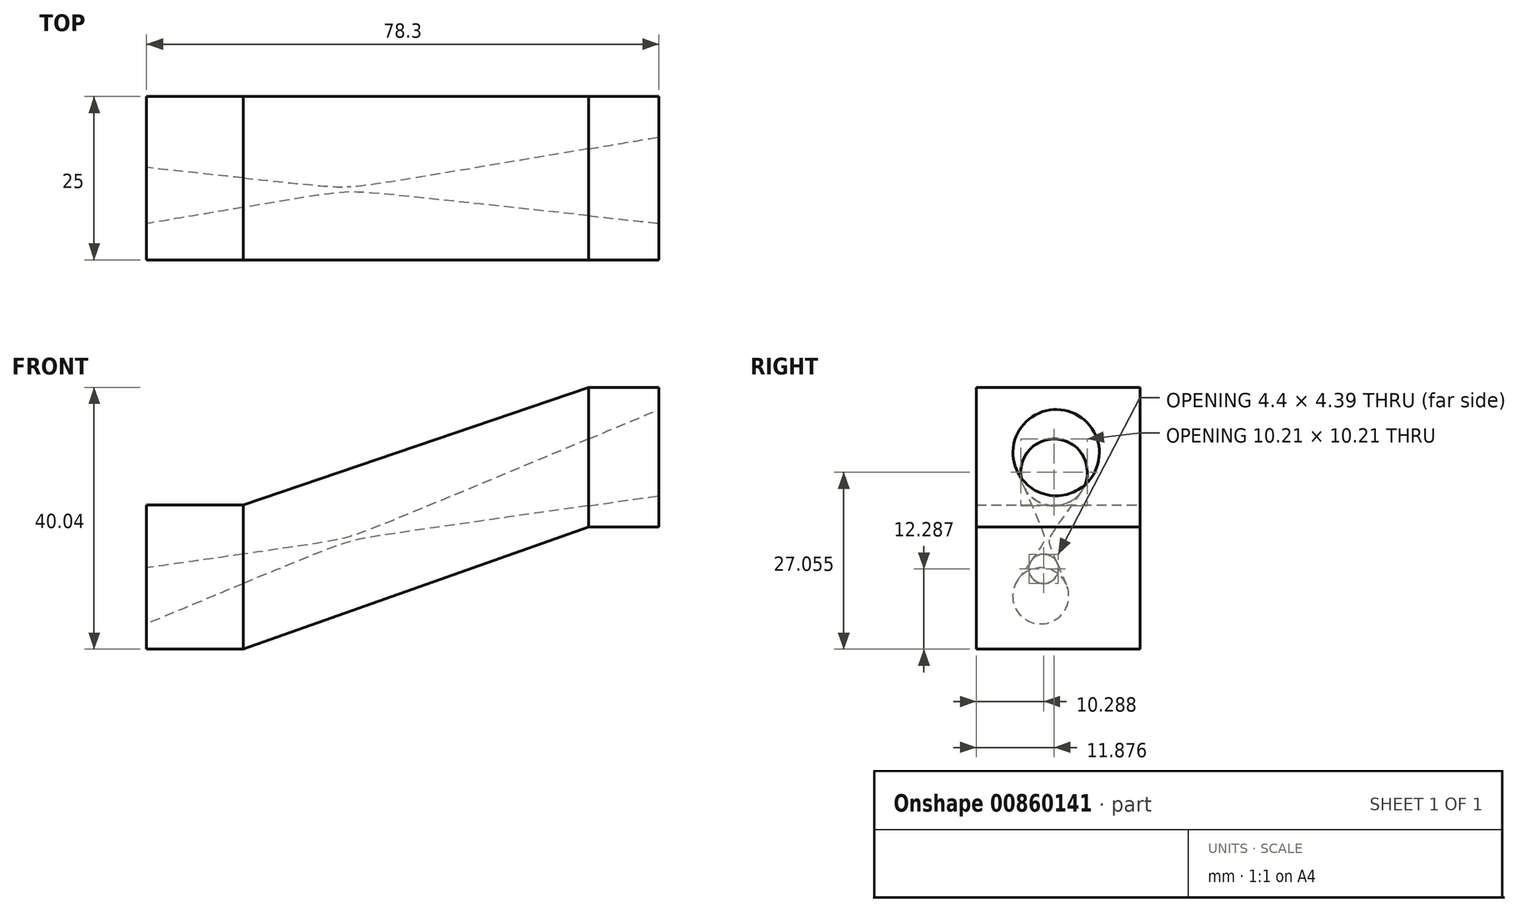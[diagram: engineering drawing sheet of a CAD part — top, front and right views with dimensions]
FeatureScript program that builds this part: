
annotation { "Feature Type Name" : "Feature", "Feature Type Description" : "" }
export const myFeature = defineFeature(function(context is Context, id is Id, definition is map)
    precondition{}
    {
        {
            var Q0;
            Q0=qCreatedBy(makeId("Front.planeOp"),FACE);
            var sketch = newSketch(context, id + "F0", { "sketchPlane" : qUnion([Q0])});
            skLineSegment(sketch, "E0.bottom", {"start": v(-43.84, 22.16) * mm, "end": v(43.84, 22.16) * mm});
            skLineSegment(sketch, "E0.top", {"start": v(-43.84, -22.16) * mm, "end": v(43.84, -22.16) * mm});
            skLineSegment(sketch, "E0.left", {"start": v(-43.84, 22.16) * mm, "end": v(-43.84, -22.16) * mm});
            skLineSegment(sketch, "E0.right", {"start": v(43.84, 22.16) * mm, "end": v(43.84, -22.16) * mm});
            skPoint(sketch, "E0.middle", {"position": v(0, 0) * mm});
            skSolve(sketch);
        }
        {
            var Q0;
            Q0=makeQuery(id+"F0.imprint","IMPRINT",FACE,{"disambiguationData":[TD([[makeQuery(id+"F0.imprint","IMPRINT",EDGE,{"derivedFrom":sQuery(id+"F0.wireOp",EDGE,"E0.bottom")}),-1.0]])]});
            var sketch = newSketch(context, id + "F1", { "sketchPlane" : qUnion([Q0])});
            skLineSegment(sketch, "E1.bottom", {"start": v(28.87, -3.33) * mm, "end": v(39.64, -3.33) * mm});
            skLineSegment(sketch, "E1.top", {"start": v(28.87, 17.99) * mm, "end": v(39.64, 17.99) * mm});
            skLineSegment(sketch, "E1.left", {"start": v(28.87, -3.33) * mm, "end": v(28.87, 17.99) * mm});
            skLineSegment(sketch, "E1.right", {"start": v(39.64, -3.33) * mm, "end": v(39.64, 17.99) * mm});
            skPoint(sketch, "E1.middle", {"position": v(34.26, 7.33) * mm});
            skSolve(sketch);
        }
        {
            var Q0;
            Q0 = qSketchRegion(id + "F1", true);
            extrude(context, id + "F2", {"entities" : qUnion([Q0]), "depth" : 25 * mm, "offsetDistance" : 25 * mm});
        }
        {
            var Q0;
            Q0=makeQuery(id+"F0.imprint","IMPRINT",FACE,{"disambiguationData":[TD([[makeQuery(id+"F0.imprint","IMPRINT",EDGE,{"derivedFrom":sQuery(id+"F0.wireOp",EDGE,"E0.bottom")}),-1.0]])]});
            var sketch = newSketch(context, id + "F3", { "sketchPlane" : qUnion([Q0])});
            skLineSegment(sketch, "E2.bottom", {"start": v(-23.92, 0) * mm, "end": v(-38.66, 0) * mm});
            skLineSegment(sketch, "E2.top", {"start": v(-23.92, -22.05) * mm, "end": v(-38.66, -22.05) * mm});
            skLineSegment(sketch, "E2.left", {"start": v(-23.92, 0) * mm, "end": v(-23.92, -22.05) * mm});
            skLineSegment(sketch, "E2.right", {"start": v(-38.66, 0) * mm, "end": v(-38.66, -22.05) * mm});
            skPoint(sketch, "E2.middle", {"position": v(-31.3, -11.02) * mm});
            skSolve(sketch);
        }
        {
            var Q0;
            Q0 = qSketchRegion(id + "F3", true);
            extrude(context, id + "F4", {"entities" : qUnion([Q0]), "depth" : 25 * mm, "offsetDistance" : 25 * mm});
        }
        {
            var Q0;
            Q0=makeQuery(id+"F4.opExtrude","SWEPT_FACE",FACE,{"disambiguationData":[OSD([sQuery(id+"F3.wireOp",EDGE,"E2.left")])]});
            var Q1;
            Q1=makeQuery(id+"F2.opExtrude","SWEPT_FACE",FACE,{"disambiguationData":[OSD([sQuery(id+"F1.wireOp",EDGE,"E1.left")])]});
            loft(context, id + "F5", {"sheetProfilesArray" : [{ "sheetProfileEntities" : qUnion([Q0]) }, { "sheetProfileEntities" : qUnion([Q1]) }]});
        }
        {
            var Q0;
            Q0=makeQuery(id+"F2.opExtrude","SWEPT_FACE",FACE,{"disambiguationData":[OSD([sQuery(id+"F1.wireOp",EDGE,"E1.right")])]});
            var sketch = newSketch(context, id + "F6", { "sketchPlane" : qUnion([Q0])});
            skCircle(sketch, "E3", {"center": v(-12.8, 8.02) * mm, "radius": 6.6 * mm});
            skSolve(sketch);
        }
        {
            var Q0;
            Q0=makeQuery(id+"F4.opExtrude","SWEPT_FACE",FACE,{"disambiguationData":[OSD([sQuery(id+"F3.wireOp",EDGE,"E2.right")])]});
            var sketch = newSketch(context, id + "F7", { "sketchPlane" : qUnion([Q0])});
            skCircle(sketch, "E4", {"center": v(15.16, -13.89) * mm, "radius": 4.29 * mm});
            skSolve(sketch);
        }
        {
            var Q0;
            Q0=makeQuery(id+"F6.imprint","IMPRINT",FACE,{"disambiguationData":[TD([[makeQuery(id+"F6.imprint","IMPRINT",EDGE,{"derivedFrom":sQuery(id+"F6.wireOp",EDGE,"E3")}),1.0]])]});
            var Q1;
            Q1=makeQuery(id+"F7.imprint","IMPRINT",FACE,{"disambiguationData":[TD([[makeQuery(id+"F7.imprint","IMPRINT",EDGE,{"derivedFrom":sQuery(id+"F7.wireOp",EDGE,"E4")}),1.0]])]});
            loft(context, id + "F8", {"operationType" : NewBodyOperationType.REMOVE, "sheetProfilesArray" : [{ "sheetProfileEntities" : qUnion([Q0]) }, { "sheetProfileEntities" : qUnion([Q1]) }]});
        }
    });
